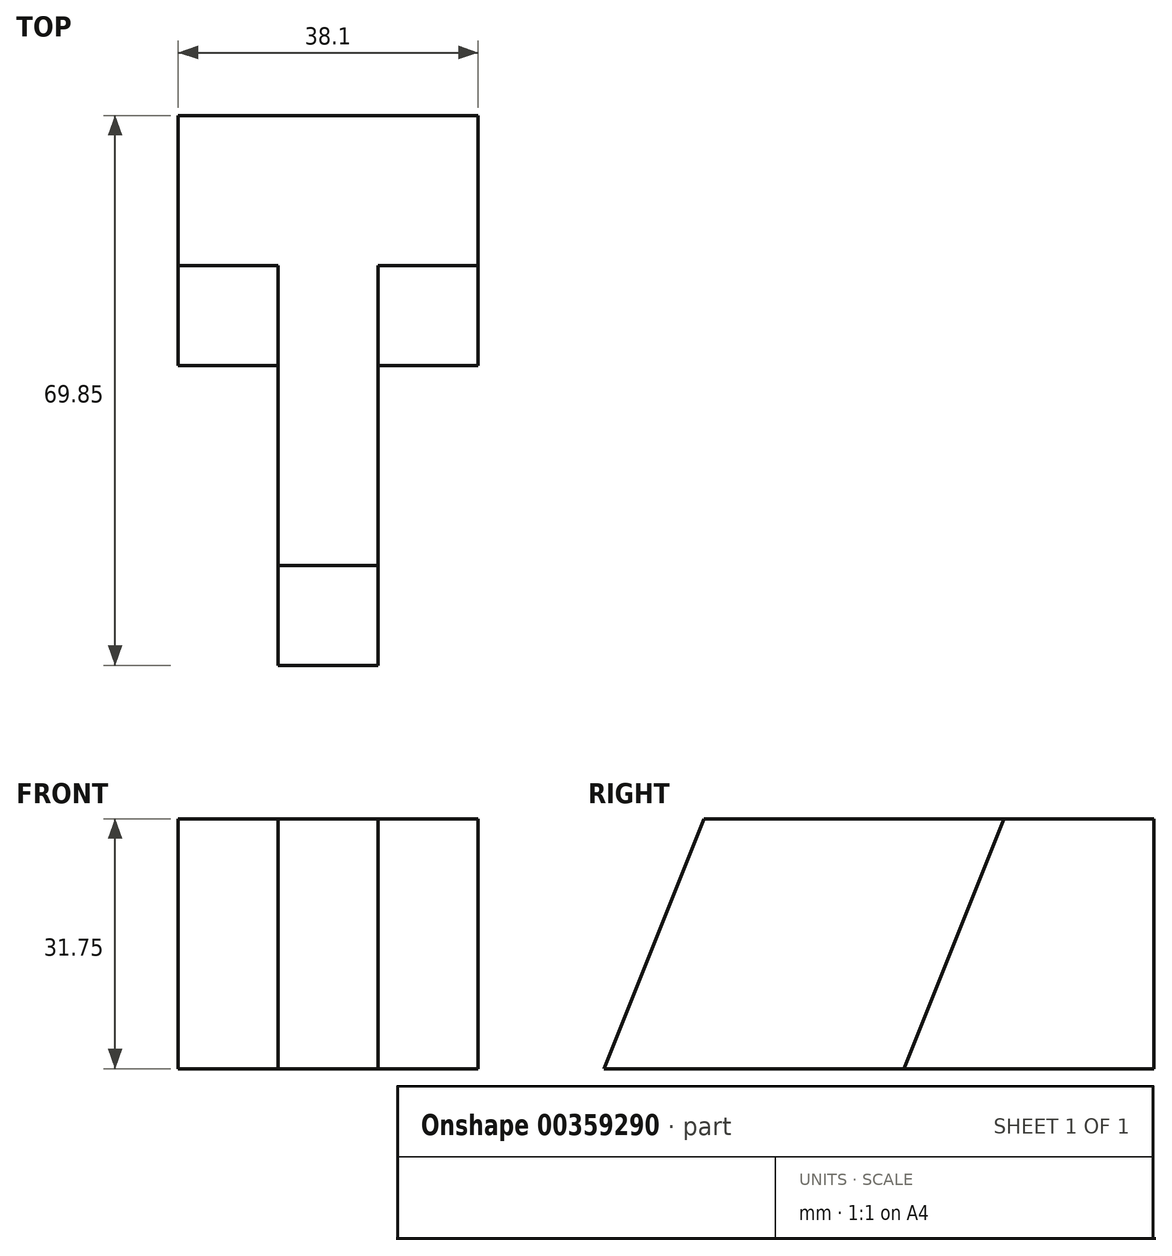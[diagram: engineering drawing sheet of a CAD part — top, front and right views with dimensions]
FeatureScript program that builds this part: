
annotation { "Feature Type Name" : "Feature", "Feature Type Description" : "" }
export const myFeature = defineFeature(function(context is Context, id is Id, definition is map)
    precondition{}
    {
        {
            var Q0;
            Q0=qCreatedBy(makeId("Top.planeOp"),FACE);
            var sketch = newSketch(context, id + "F0", { "sketchPlane" : qUnion([Q0])});
            skLineSegment(sketch, "E0", {"start": v(0, 0) * mm, "end": v(0, 38.1) * mm});
            skLineSegment(sketch, "E1", {"start": v(0, 38.1) * mm, "end": v(-12.7, 38.1) * mm});
            skLineSegment(sketch, "E2", {"start": v(-12.7, 38.1) * mm, "end": v(-12.7, 69.85) * mm});
            skLineSegment(sketch, "E3", {"start": v(-12.7, 69.85) * mm, "end": v(25.4, 69.85) * mm});
            skLineSegment(sketch, "E4", {"start": v(25.4, 69.85) * mm, "end": v(25.4, 38.1) * mm});
            skLineSegment(sketch, "E5", {"start": v(25.4, 38.1) * mm, "end": v(12.7, 38.1) * mm});
            skLineSegment(sketch, "E6", {"start": v(12.7, 38.1) * mm, "end": v(12.7, 0) * mm});
            skLineSegment(sketch, "E7", {"start": v(12.7, 0) * mm, "end": v(0, 0) * mm});
            skSolve(sketch);
        }
        {
            var Q0;
            Q0 = qSketchRegion(id + "F0", true);
            extrude(context, id + "F1", {"entities" : qUnion([Q0]), "depth" : 31.75 * mm});
        }
        {
            var Q0;
            Q0=makeQuery(id+"F1.opExtrude","SWEPT_FACE",FACE,{"disambiguationData":[OSD([sQuery(id+"F0.wireOp",EDGE,"E0")])]});
            var sketch = newSketch(context, id + "F2", { "sketchPlane" : qUnion([Q0])});
            skLineSegment(sketch, "E8", {"start": v(0, 31.75) * mm, "end": v(0, 0) * mm});
            skLineSegment(sketch, "E9", {"start": v(0, 31.75) * mm, "end": v(-12.7, 31.75) * mm});
            skLineSegment(sketch, "E10", {"start": v(-12.7, 31.75) * mm, "end": v(0, 0) * mm});
            skSolve(sketch);
        }
        {
            var Q0;
            Q0 = qSketchRegion(id + "F2", true);
            extrude(context, id + "F3", {"entities" : qUnion([Q0]), "operationType" : NewBodyOperationType.REMOVE, "oppositeDirection" : true, "depth" : 25.4 * mm});
        }
        {
            var Q0;
            Q0=makeQuery(id+"F1.opExtrude","SWEPT_FACE",FACE,{"disambiguationData":[OSD([sQuery(id+"F0.wireOp",EDGE,"E2")])]});
            var sketch = newSketch(context, id + "F4", { "sketchPlane" : qUnion([Q0])});
            skLineSegment(sketch, "E11", {"start": v(-38.1, 31.75) * mm, "end": v(-38.1, 0) * mm});
            skLineSegment(sketch, "E12", {"start": v(-38.1, 0) * mm, "end": v(-50.8, 31.75) * mm});
            skLineSegment(sketch, "E13", {"start": v(-50.8, 31.75) * mm, "end": v(-38.1, 31.75) * mm});
            skSolve(sketch);
        }
        {
            var Q0;
            Q0 = qSketchRegion(id + "F4", true);
            extrude(context, id + "F5", {"entities" : qUnion([Q0]), "operationType" : NewBodyOperationType.REMOVE, "oppositeDirection" : true, "depth" : 12.7 * mm});
        }
        {
            var Q0;
            Q0=makeQuery(id+"F1.opExtrude","SWEPT_FACE",FACE,{"disambiguationData":[OSD([sQuery(id+"F0.wireOp",EDGE,"E4")])]});
            var sketch = newSketch(context, id + "F6", { "sketchPlane" : qUnion([Q0])});
            skLineSegment(sketch, "E14", {"start": v(38.1, 31.75) * mm, "end": v(38.1, 0) * mm});
            skLineSegment(sketch, "E15", {"start": v(38.1, 0) * mm, "end": v(50.8, 31.75) * mm});
            skLineSegment(sketch, "E16", {"start": v(50.8, 31.75) * mm, "end": v(38.1, 31.75) * mm});
            skSolve(sketch);
        }
        {
            var Q0;
            Q0 = qSketchRegion(id + "F6", true);
            extrude(context, id + "F7", {"entities" : qUnion([Q0]), "operationType" : NewBodyOperationType.REMOVE, "oppositeDirection" : true, "depth" : 12.7 * mm});
        }
    });
